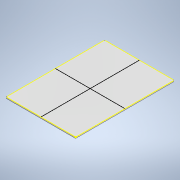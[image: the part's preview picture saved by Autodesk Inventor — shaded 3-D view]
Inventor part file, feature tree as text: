
AUTODESK INVENTOR PART (.ipt)
format: ipt  version: 2020.3 (Build 243373000, 373)  size: 130,048 bytes
history: native  units: mm
features: sketch x2, extrude x2, fillet x2
ambient origin geometry x8: Origin, YZ Plane, XZ Plane, XY Plane, X Axis, Y Axis, Z Axis, Center Point
bodies: Body1 (feature_tree)
feature tree (6):
  sketch  "Sketch1"  dims[d30=210.0mm d31=297.0mm]
  extrude  "Extrusion6"  Depth=297.0mm
  extrude  "Extrusion7"  Depth=85.0mm
  fillet  "Fillet3"  Radius=4.0mm
  fillet  "Fillet4"  Radius=4.0mm
  sketch  "Sketch3"  dims[d34=164.0mm d35=85.0mm d36=4.0mm d37=0.0mm d38=4.0mm d39=0.0mm d40=2.0mm d41=8.0mm d42=106.0mm d43=23.0mm d8=0.5mm d9=0.872665mm d10=0.5mm d11=0.872665mm]
